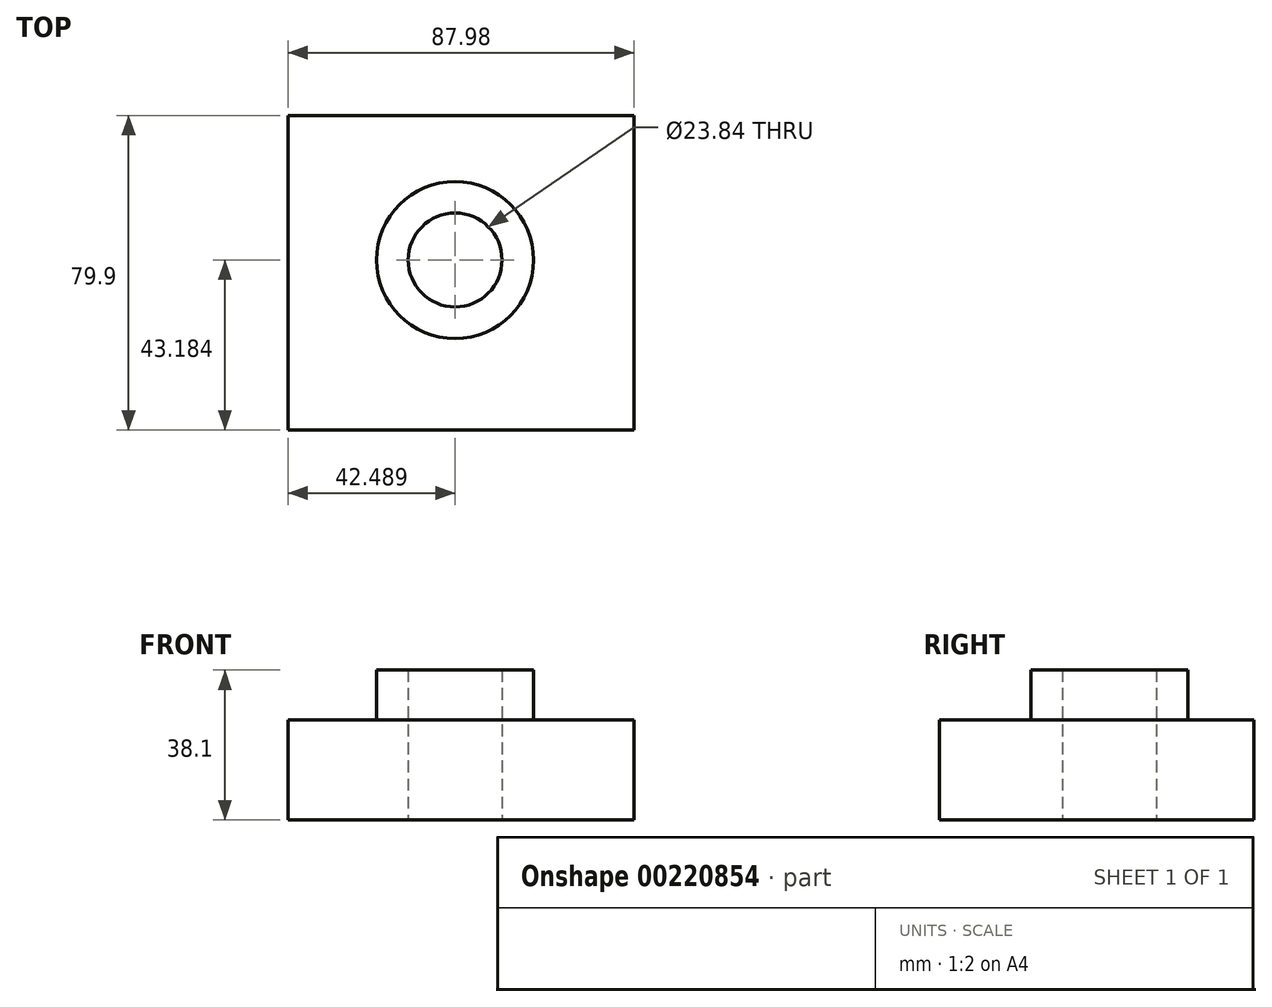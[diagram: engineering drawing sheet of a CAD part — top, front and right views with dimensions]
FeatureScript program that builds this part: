
annotation { "Feature Type Name" : "Feature", "Feature Type Description" : "" }
export const myFeature = defineFeature(function(context is Context, id is Id, definition is map)
    precondition{}
    {
        {
            var Q0;
            Q0=qCreatedBy(makeId("Top.planeOp"),FACE);
            var sketch = newSketch(context, id + "F0", { "sketchPlane" : qUnion([Q0])});
            skLineSegment(sketch, "E0.bottom", {"start": v(-37.64, 38.9) * mm, "end": v(50.34, 38.9) * mm});
            skLineSegment(sketch, "E0.top", {"start": v(-37.64, -40.99) * mm, "end": v(50.34, -40.99) * mm});
            skLineSegment(sketch, "E0.left", {"start": v(-37.64, 38.9) * mm, "end": v(-37.64, -40.99) * mm});
            skLineSegment(sketch, "E0.right", {"start": v(50.34, 38.9) * mm, "end": v(50.34, -40.99) * mm});
            skCircle(sketch, "E1", {"center": v(4.85, 2.2) * mm, "radius": 11.92 * mm});
            skCircle(sketch, "E2", {"center": v(4.85, 2.2) * mm, "radius": 19.95 * mm});
            skSolve(sketch);
        }
        {
            var Q0;
            Q0=makeQuery(id+"F0.imprint","IMPRINT",FACE,{"disambiguationData":[TD([[makeQuery(id+"F0.imprint","IMPRINT",EDGE,{"derivedFrom":sQuery(id+"F0.wireOp",EDGE,"E1")}),-1.0]])]});
            extrude(context, id + "F1", {"entities" : qUnion([Q0]), "depth" : 38.1 * mm});
        }
        {
            var Q0;
            Q0=makeQuery(id+"F0.imprint","IMPRINT",FACE,{"disambiguationData":[TD([[makeQuery(id+"F0.imprint","IMPRINT",EDGE,{"derivedFrom":sQuery(id+"F0.wireOp",EDGE,"E0.bottom")}),-1.0]])]});
            extrude(context, id + "F2", {"entities" : qUnion([Q0]), "operationType" : NewBodyOperationType.ADD, "depth" : 25.4 * mm});
        }
    });
